# Revit family: Faucet-Two_Handle-American_Standard-Berwick-7430.8XX_Series
name_source: partatom
category: Plumbing Fixtures
revit_build: Autodesk Revit 2014 (Build: 20130308_1515(x64)
units: mm (PartAtom-declared; Revit-internal decimal feet)

## types (2) — shared parameters
Assembly Code = D2020300
CW Connection = Yes
CWFU = 1.5
Cold Water Connection Diameter = 3/4"
Cold Water Connection Radius = 3/8"
Default Elevation = 0"
Description = Berwick Two-Handle Widespread Lavatory Faucet.
Flow Rate = 1.5 GPM
HW Connection = Yes
HWFU = 1.5
Height = 11 1/8"
Hot Water Connection Diameter = 3/4"
Hot Water Connection Radius = 3/8"
Installation Type = Deck Mounted
Length = 10"
Manufacturer = American Standard
Material = Brass-American Standard-002-Polished Chrome
Price = Prices may vary. Please consult Manufacturer Representative for most up-to-date price list.
Product Documentation Link = https://www.americanstandard-us.com
Product Page URL = https://www.americanstandard-us.com
Revised Date = 02/08/2017
URL = http://www.americanstandard-us.com
Vent Connection = No
Warranty Information = 1 Year (Limited)
Waste Connection = No
Width = 8 3/8"
zero-valued in all types: WFU

## per-type parameters (varying)
| type | ADA Compliant | Cross Handles | Lever Handles | Model | Specification |
| 7430.801 | Yes | No | Yes | 7430.801 | Berwick Widespread. Metal Speed Connect Pop-up drain. Metal Lever handles. |
| 7430.821 | No | Yes | No | 7403.821 | Berwick Widespread. Metal Speed Connect Pop-up drain. Metal Cross handles. |

## geometry (parser evidence)
native form markers: Sweep x1
no freeform markers — native parametric forms only
